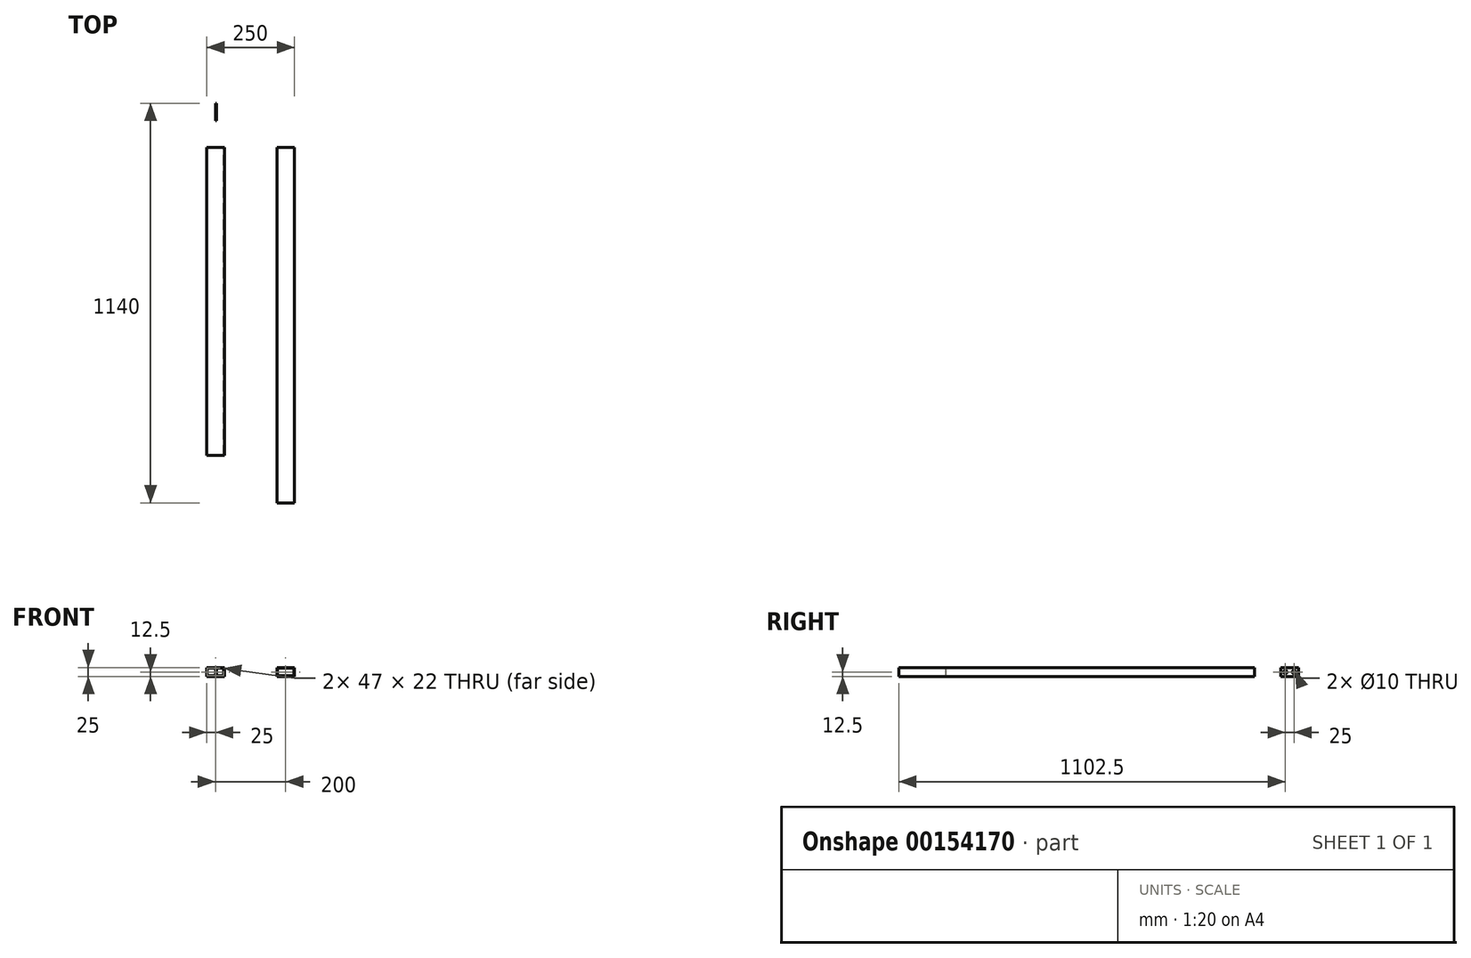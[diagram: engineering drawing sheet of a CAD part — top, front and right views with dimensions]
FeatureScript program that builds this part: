
annotation { "Feature Type Name" : "Feature", "Feature Type Description" : "" }
export const myFeature = defineFeature(function(context is Context, id is Id, definition is map)
    precondition{}
    {
        {
            var Q0;
            Q0=qCreatedBy(makeId("Front.planeOp"),FACE);
            var sketch = newSketch(context, id + "F0", { "sketchPlane" : qUnion([Q0])});
            skLineSegment(sketch, "E0.bottom", {"start": v(25, -12.5) * mm, "end": v(-25, -12.5) * mm});
            skLineSegment(sketch, "E0.top", {"start": v(25, 12.5) * mm, "end": v(-25, 12.5) * mm});
            skLineSegment(sketch, "E0.left", {"start": v(25, -12.5) * mm, "end": v(25, 12.5) * mm});
            skLineSegment(sketch, "E0.right", {"start": v(-25, -12.5) * mm, "end": v(-25, 12.5) * mm});
            skPoint(sketch, "E0.middle", {"position": v(0, 0) * mm});
            skLineSegment(sketch, "E1.bottom", {"start": v(23.5, -11) * mm, "end": v(-23.5, -11) * mm});
            skLineSegment(sketch, "E1.top", {"start": v(23.5, 11) * mm, "end": v(-23.5, 11) * mm});
            skLineSegment(sketch, "E1.left", {"start": v(23.5, -11) * mm, "end": v(23.5, 11) * mm});
            skLineSegment(sketch, "E1.right", {"start": v(-23.5, -11) * mm, "end": v(-23.5, 11) * mm});
            skSolve(sketch);
        }
        {
            var Q0;
            Q0=makeQuery(id+"F0.imprint","IMPRINT",FACE,{"disambiguationData":[TD([[makeQuery(id+"F0.imprint","IMPRINT",EDGE,{"derivedFrom":sQuery(id+"F0.wireOp",EDGE,"E0.bottom")}),-1.0]])]});
            extrude(context, id + "F1", {"entities" : qUnion([Q0]), "depth" : 880 * mm});
        }
        {
            var Q0;
            Q0=qCreatedBy(makeId("Right.planeOp"),FACE);
            var sketch = newSketch(context, id + "F2", { "sketchPlane" : qUnion([Q0])});
            skLineSegment(sketch, "E2", {"start": v(0, 0) * mm, "end": v(100, 0) * mm, "construction": true});
            skLineSegment(sketch, "E3.bottom", {"start": v(125, -12.5) * mm, "end": v(75, -12.5) * mm});
            skLineSegment(sketch, "E3.top", {"start": v(125, 12.5) * mm, "end": v(75, 12.5) * mm});
            skLineSegment(sketch, "E3.left", {"start": v(125, -12.5) * mm, "end": v(125, 12.5) * mm});
            skLineSegment(sketch, "E3.right", {"start": v(75, -12.5) * mm, "end": v(75, 12.5) * mm});
            skPoint(sketch, "E3.middle", {"position": v(100, 0) * mm});
            skLineSegment(sketch, "E4", {"start": v(125, 0) * mm, "end": v(112.5, 0) * mm, "construction": true});
            skPoint(sketch, "E4.endSnap0", {"position": v(75, 0) * mm});
            skPoint(sketch, "E5", {"position": v(112.5, 0) * mm});
            skLineSegment(sketch, "E6", {"start": v(75, 0) * mm, "end": v(87.5, 0) * mm, "construction": true});
            skPoint(sketch, "E7", {"position": v(87.5, 0) * mm});
            skSolve(sketch);
        }
        {
            var Q0;
            Q0 = qSketchRegion(id + "F2", true);
            extrude(context, id + "F3", {"entities" : qUnion([Q0]), "depth" : 3 * mm});
        }
        {
            var Q0;
            Q0=sQuery(id+"F2.wireOp",VERTEX,"E7");
            var Q1;
            Q1=sQuery(id+"F2.wireOp",VERTEX,"E5");
            var Q2;
            Q2=makeQuery(id+"F3.opExtrude","SWEPT_BODY",BODY,{"disambiguationData":[OSD([sQuery(id+"F2.wireOp",EDGE,"E3.bottom"),sQuery(id+"F2.wireOp",EDGE,"E3.top"),sQuery(id+"F2.wireOp",EDGE,"E3.left"),sQuery(id+"F2.wireOp",EDGE,"E3.right")])]});
            hole(context, id + "F4", {"style" : HoleStyle.SIMPLE, "endStyle" : HoleEndStyle.THROUGH, "oppositeDirection" : true, "holeDiameter" : 10 * mm, "locations" : qUnion([Q0, Q1]), "scope" : qUnion([Q2]), "isTappedThrough" : true});
        }
        {
            var Q0;
            Q0=qCreatedBy(makeId("Front.planeOp"),FACE);
            var sketch = newSketch(context, id + "F5", { "sketchPlane" : qUnion([Q0])});
            skLineSegment(sketch, "E8.bottom", {"start": v(225, -12.5) * mm, "end": v(175, -12.5) * mm});
            skLineSegment(sketch, "E8.top", {"start": v(225, 12.5) * mm, "end": v(175, 12.5) * mm});
            skLineSegment(sketch, "E8.left", {"start": v(225, -12.5) * mm, "end": v(225, 12.5) * mm});
            skLineSegment(sketch, "E8.right", {"start": v(175, -12.5) * mm, "end": v(175, 12.5) * mm});
            skPoint(sketch, "E8.middle", {"position": v(200, 0) * mm});
            skLineSegment(sketch, "E9.bottom", {"start": v(223.5, -11) * mm, "end": v(176.5, -11) * mm});
            skLineSegment(sketch, "E9.top", {"start": v(223.5, 11) * mm, "end": v(176.5, 11) * mm});
            skLineSegment(sketch, "E9.left", {"start": v(223.5, -11) * mm, "end": v(223.5, 11) * mm});
            skLineSegment(sketch, "E9.right", {"start": v(176.5, -11) * mm, "end": v(176.5, 11) * mm});
            skLineSegment(sketch, "E10", {"start": v(200, 0) * mm, "end": v(0, 0) * mm, "construction": true});
            skSolve(sketch);
        }
        {
            var Q0;
            Q0 = qSketchRegion(id + "F5", true);
            extrude(context, id + "F6", {"entities" : qUnion([Q0]), "depth" : 1015 * mm});
        }
    });
